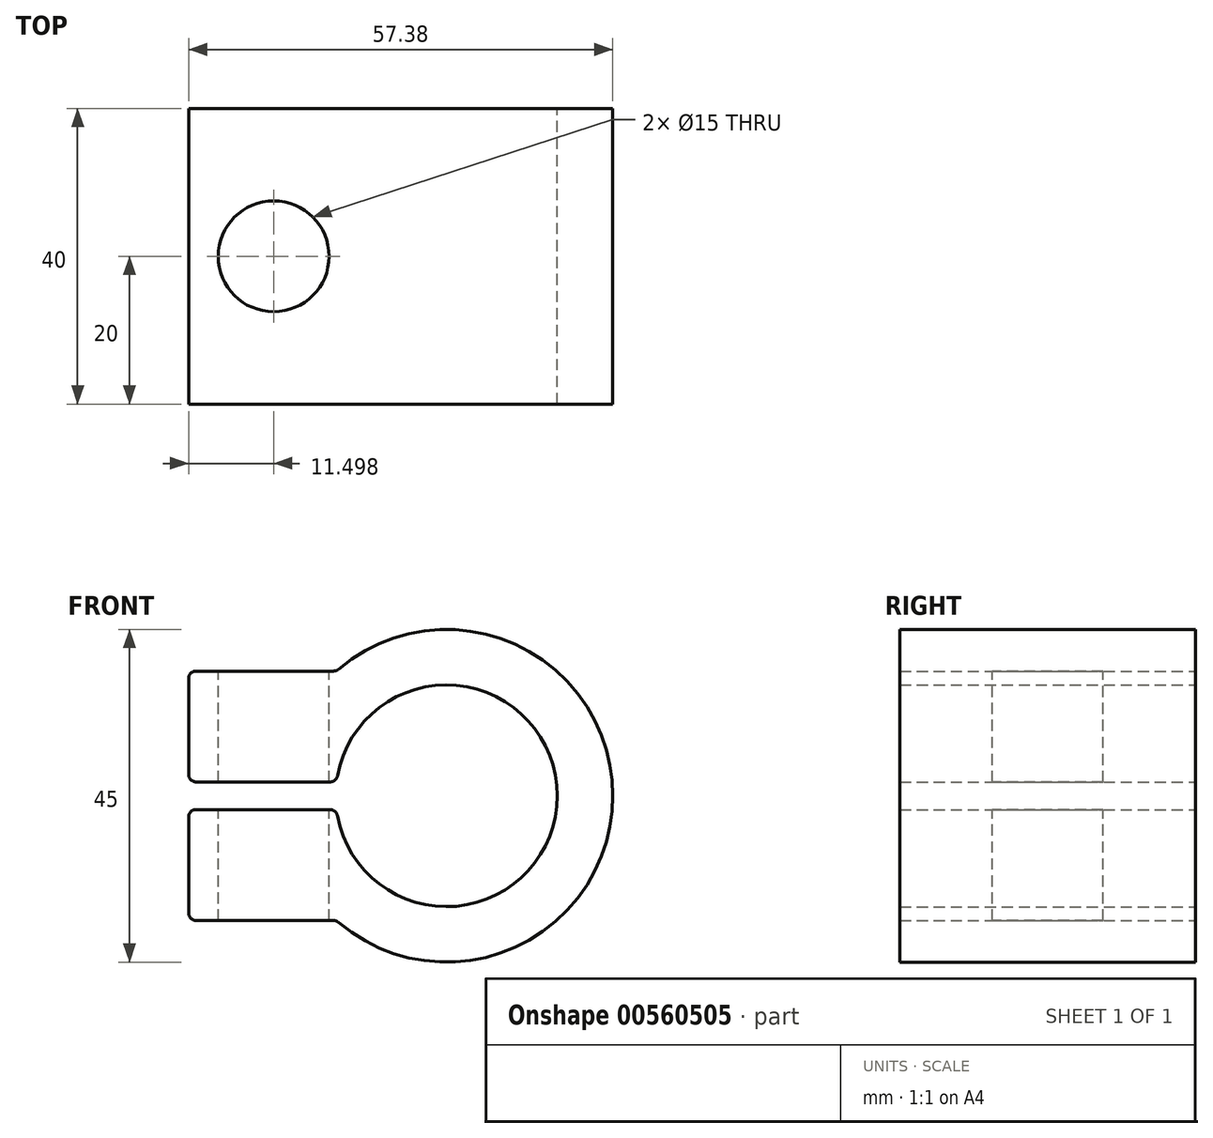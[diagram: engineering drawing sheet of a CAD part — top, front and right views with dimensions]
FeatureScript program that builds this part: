
annotation { "Feature Type Name" : "Feature", "Feature Type Description" : "" }
export const myFeature = defineFeature(function(context is Context, id is Id, definition is map)
    precondition{}
    {
        {
            var Q0;
            Q0=qCreatedBy(makeId("Front.planeOp"),FACE);
            var sketch = newSketch(context, id + "F0", { "sketchPlane" : qUnion([Q0])});
            skLineSegment(sketch, "E0", {"start": v(-34.88, 2.88) * mm, "end": v(-34.88, 15.88) * mm});
            skLineSegment(sketch, "E1", {"start": v(-33.88, 16.88) * mm, "end": v(-15.26, 16.88) * mm});
            skLineSegment(sketch, "E2", {"start": v(-33.88, 1.88) * mm, "end": v(-15.74, 1.88) * mm});
            skArc(sketch, "E3", {"start": v(22.5, 0) * mm, "mid": v(9.42, 20.43) * mm, "end": v(-14.6, 17.11) * mm});
            skPoint(sketch, "E4.visualSharp", {"position": v(-14.88, 16.88) * mm});
            skArc(sketch, "E4.filletArc", {"start": v(-15.26, 16.88) * mm, "mid": v(-14.9, 16.94) * mm, "end": v(-14.6, 17.11) * mm});
            skPoint(sketch, "E5.visualSharp", {"position": v(-34.88, 16.88) * mm});
            skArc(sketch, "E5.filletArc", {"start": v(-33.88, 16.88) * mm, "mid": v(-34.59, 16.58) * mm, "end": v(-34.88, 15.88) * mm});
            skPoint(sketch, "E6.visualSharp", {"position": v(-34.88, 1.88) * mm});
            skArc(sketch, "E6.filletArc", {"start": v(-34.88, 2.88) * mm, "mid": v(-34.59, 2.17) * mm, "end": v(-33.88, 1.87) * mm});
            skArc(sketch, "E7", {"start": v(-14.76, 2.7) * mm, "mid": v(1.35, 14.94) * mm, "end": v(15, 0) * mm});
            skLineSegment(sketch, "E8", {"start": v(15, 0) * mm, "end": v(22.5, 0) * mm});
            skPoint(sketch, "E9.visualSharp", {"position": v(-14.88, 1.88) * mm});
            skArc(sketch, "E9.filletArc", {"start": v(-15.74, 1.88) * mm, "mid": v(-15.1, 2.1) * mm, "end": v(-14.76, 2.7) * mm});
            skSolve(sketch);
        }
        {
            var Q0;
            Q0 = qSketchRegion(id + "F0", true);
            extrude(context, id + "F1", {"entities" : qUnion([Q0]), "depth" : 40 * mm, "offsetDistance" : 25 * mm});
        }
        {
            var Q0;
            Q0=makeQuery(id+"F1.opExtrude","SWEPT_BODY",BODY,{"disambiguationData":[OSD([sQuery(id+"F0.wireOp",EDGE,"E0"),sQuery(id+"F0.wireOp",EDGE,"E1"),sQuery(id+"F0.wireOp",EDGE,"E2"),sQuery(id+"F0.wireOp",EDGE,"E3"),sQuery(id+"F0.wireOp",EDGE,"E4.filletArc"),sQuery(id+"F0.wireOp",EDGE,"E5.filletArc"),sQuery(id+"F0.wireOp",EDGE,"E6.filletArc"),sQuery(id+"F0.wireOp",EDGE,"E7"),sQuery(id+"F0.wireOp",EDGE,"E8"),sQuery(id+"F0.wireOp",EDGE,"E9.filletArc")])]});
            var Q1;
            Q1=makeQuery(id+"F1.opExtrude","SWEPT_FACE",FACE,{"disambiguationData":[OSD([sQuery(id+"F0.wireOp",EDGE,"E8")])]});
            mirror(context, id + "F2", {"operationType" : NewBodyOperationType.ADD, "entities" : qUnion([Q0]), "mirrorPlane" : qUnion([Q1])});
        }
        {
            var Q0;
            Q0=makeQuery(id+"F1.opExtrude","SWEPT_FACE",FACE,{"disambiguationData":[OSD([sQuery(id+"F0.wireOp",EDGE,"E1")])]});
            var sketch = newSketch(context, id + "F3", { "sketchPlane" : qUnion([Q0])});
            skCircle(sketch, "E10", {"center": v(-23.38, -20) * mm, "radius": 7.5 * mm});
            skPoint(sketch, "E10.centerSnap0", {"position": v(-15.26, -20) * mm});
            skSolve(sketch);
        }
        {
            var Q0;
            Q0 = qSketchRegion(id + "F3", true);
            extrude(context, id + "F4", {"entities" : qUnion([Q0]), "operationType" : NewBodyOperationType.REMOVE, "oppositeDirection" : true, "depth" : 45 * mm, "offsetDistance" : 25 * mm});
        }
    });
